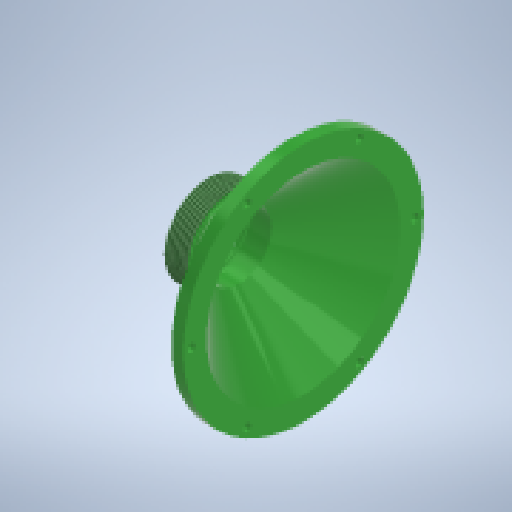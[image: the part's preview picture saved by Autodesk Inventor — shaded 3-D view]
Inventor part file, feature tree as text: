
AUTODESK INVENTOR PART (.ipt)
format: ipt  version: 2023 (Build 270158000, 158)  size: 335,872 bytes
history: native  units: mm
features: sketch x2, revolve x1, thread x1, hole x1, pattern_circular x1
ambient origin geometry x8: Origin, YZ Plane, XZ Plane, XY Plane, X Axis, Y Axis, Z Axis, Center Point
bodies: Solid1 (feature_tree)
feature tree (6):
  revolve  "Revolution1"  Angle=90.0deg
  thread  "Thread4"  [1 undecoded]
  hole  "Hole1"  [1 undecoded]
  pattern_circular  "Circular Pattern1"  [2 undecoded]
  sketch  "Sketch1"  dims[d2=28.0mm d12=90.0deg d19=103.0mm]
  sketch  "Sketch2"  dims[d20=83.0mm d21=5.0mm d22=1.6mm d23=135.0deg d24=2.0mm d25=1.0mm d26=1.0mm d27=3.0mm d28=1.5mm d29=38.0mm d30=2.0mm d32=10.0mm d33=9.0mm d34=10.0mm d35=0.0mm d36=48.0mm d37=3.5mm d38=6.0mm d39=4.0mm d40=2.0mm d41=90.0deg d42=8.0mm d43=0.0mm d44=60.0mm d45=360.0deg]
note: 4 required parameter values undecoded (feature->parameter linkage not recoverable at this tier; creation-order binding heuristic only, values carry confidence <= 0.55)
